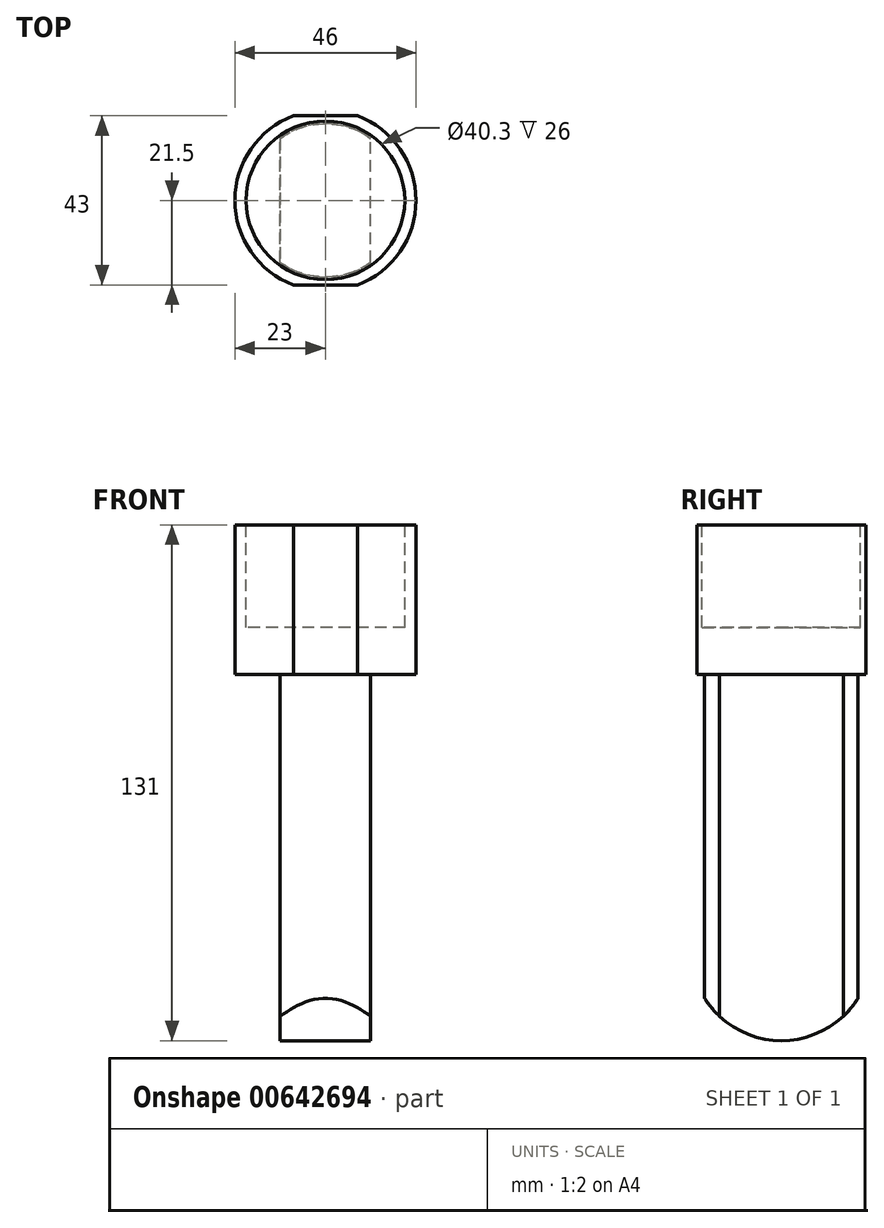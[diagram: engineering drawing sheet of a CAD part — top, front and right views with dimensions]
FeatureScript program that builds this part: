
annotation { "Feature Type Name" : "Feature", "Feature Type Description" : "" }
export const myFeature = defineFeature(function(context is Context, id is Id, definition is map)
    precondition{}
    {
        {
            var Q0;
            Q0=qCreatedBy(makeId("Top.planeOp"),FACE);
            var sketch = newSketch(context, id + "F0", { "sketchPlane" : qUnion([Q0])});
            skArc(sketch, "E0", {"start": v(-8.17, 21.5) * mm, "mid": v(-23, 0) * mm, "end": v(-8.17, -21.5) * mm});
            skLineSegment(sketch, "E1", {"start": v(-8.17, 21.5) * mm, "end": v(8.17, 21.5) * mm});
            skLineSegment(sketch, "E2.MirrorCS", {"start": v(-8.17, -21.5) * mm, "end": v(8.17, -21.5) * mm});
            skArc(sketch, "E3.trimOffspring", {"start": v(8.17, -21.5) * mm, "mid": v(23, 0) * mm, "end": v(8.17, 21.5) * mm});
            skSolve(sketch);
        }
        {
            var Q0;
            Q0 = qSketchRegion(id + "F0", true);
            extrude(context, id + "F1", {"entities" : qUnion([Q0]), "depth" : 38 * mm, "offsetDistance" : 25 * mm});
        }
        {
            var Q0;
            Q0=makeQuery(id+"F1.opExtrude","CAP_FACE",FACE,{"disambiguationData":[OSD([sQuery(id+"F0.wireOp",EDGE,"E0"),sQuery(id+"F0.wireOp",EDGE,"E1"),sQuery(id+"F0.wireOp",EDGE,"E2.MirrorCS"),sQuery(id+"F0.wireOp",EDGE,"E3.trimOffspring")])],"isStart":false});
            var sketch = newSketch(context, id + "F2", { "sketchPlane" : qUnion([Q0])});
            skCircle(sketch, "E4", {"center": v(0, 0) * mm, "radius": 20.15 * mm});
            skSolve(sketch);
        }
        {
            var Q0;
            Q0 = qSketchRegion(id + "F2", true);
            extrude(context, id + "F3", {"entities" : qUnion([Q0]), "operationType" : NewBodyOperationType.REMOVE, "oppositeDirection" : true, "depth" : 26 * mm, "offsetDistance" : 25 * mm});
        }
        {
            var Q0;
            Q0=makeQuery(id+"F1.opExtrude","CAP_FACE",FACE,{"disambiguationData":[OSD([sQuery(id+"F0.wireOp",EDGE,"E0"),sQuery(id+"F0.wireOp",EDGE,"E1"),sQuery(id+"F0.wireOp",EDGE,"E2.MirrorCS"),sQuery(id+"F0.wireOp",EDGE,"E3.trimOffspring")])],"isStart":true});
            var sketch = newSketch(context, id + "F4", { "sketchPlane" : qUnion([Q0])});
            skArc(sketch, "E5", {"start": v(-11.5, -15.75) * mm, "mid": v(0, -19.5) * mm, "end": v(11.5, -15.75) * mm});
            skLineSegment(sketch, "E6", {"start": v(-11.5, 15.75) * mm, "end": v(-11.5, -15.75) * mm});
            skLineSegment(sketch, "E7.MirrorCS", {"start": v(11.5, 15.75) * mm, "end": v(11.5, -15.75) * mm});
            skArc(sketch, "E8.trimOffspring", {"start": v(11.5, 15.75) * mm, "mid": v(0, 19.5) * mm, "end": v(-11.5, 15.75) * mm});
            skSolve(sketch);
        }
        {
            var Q0;
            Q0 = qSketchRegion(id + "F4", true);
            extrude(context, id + "F5", {"entities" : qUnion([Q0]), "operationType" : NewBodyOperationType.ADD, "depth" : 93 * mm, "offsetDistance" : 25 * mm});
        }
        {
            var Q0;
            Q0=makeQuery(id+"F5.opExtrude","SWEPT_FACE",FACE,{"disambiguationData":[OSD([sQuery(id+"F4.wireOp",EDGE,"E6")])]});
            var sketch = newSketch(context, id + "F6", { "sketchPlane" : qUnion([Q0])});
            skArc(sketch, "E9", {"start": v(-22.17, -76.13) * mm, "mid": v(0.9, -92.98) * mm, "end": v(22.58, -74.38) * mm});
            skLineSegment(sketch, "E10", {"start": v(-22.17, -76.13) * mm, "end": v(-29.64, -101.4) * mm});
            skLineSegment(sketch, "E11", {"start": v(-29.64, -101.4) * mm, "end": v(27.82, -100.33) * mm});
            skLineSegment(sketch, "E12", {"start": v(27.82, -100.33) * mm, "end": v(22.58, -74.38) * mm});
            skSolve(sketch);
        }
        {
            var Q0;
            Q0 = qSketchRegion(id + "F6", true);
            extrude(context, id + "F7", {"entities" : qUnion([Q0]), "operationType" : NewBodyOperationType.REMOVE, "endBound" : BoundingType.THROUGH_ALL, "oppositeDirection" : true, "depth" : 25 * mm, "offsetDistance" : 25 * mm});
        }
    });
